# Revit family: Heater-QMark-Thermazone_Thin_Series
name_source: partatom
category: Mechanical Equipment
units: mm (PartAtom-declared; Revit-internal decimal feet)

## family parameters
Classification = None
Cut with Voids When Loaded = No
Host = Face
OmniClass Number = 23.75.70.17.17
OmniClass Title = Radiation Panels
Part Type = Normal
Room Calculation Point = No
Round Connector Dimension = Use Diameter
Shared = No

## types (1)
- Not a Type - Load Type Catalog
    Amps = 0 A
    Assembly Code = D3060300
    Default Elevation = 0' - 0"
    Depth = 0' - 8"
    Description = Infrared Heaters for Industrial/Commercial/Residential
    Frequency = 60 Hz
    Height = 0' - 9"
    Infrared Material = Paint - Berko - Powder Coated Black
    Instruction Sheet Link = https://www.marleymep.com
    Keynote = 15500
    Length = 3' - 6"
    Manufacturer = Marley® Engineered Products
    Model = Noy a Type - Load Type Catalog
    Number of Poles = 1
    Phase = 1
    Power Factor = 1
    Product Documentation Link = https://www.marleymep.com
    Product Name = Thermazone Thin Series - Commercial/Residential Infrared Heater
    Product Page URL = https://www.marleymep.com
    Total Heating Capacity = 0.0 Btu/h
    URL = https://www.marleymep.com
    Version = 2020 - v1.0a
    Voltage = 0 V
    Watts = 0 W

## geometry (parser evidence)
native form markers: Sweep x2
no freeform markers — native parametric forms only
